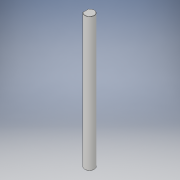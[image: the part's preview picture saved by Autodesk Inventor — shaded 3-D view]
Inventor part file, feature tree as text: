
AUTODESK INVENTOR PART (.ipt)
format: ipt  version: 2019 (Build 230136000, 136)  size: 122,880 bytes
history: native  units: in
note: dims shown in document units (in); Inventor stores cm internally (conversion verified against a paired STEP export)
features: chamfer x1, direct_edit x1, extrude x1, fillet x1, sketch x1, projected_geometry x1, other x1
ambient origin geometry x8: Origin, YZ Plane, XZ Plane, XY Plane, X Axis, Y Axis, Z Axis, Center Point
bodies: Solid1 (feature_tree)
feature tree (7):
  chamfer  "Chamfer1"  Distance=0.505in
  direct_edit  "Direct Edit2"
  extrude  "Extrusion1"  Depth=0.005in
  fillet  "Fillet1"  [1 undecoded]
  sketch  "Sketch1"  dims[d3=-0.005in d4=0.505in d5=0.0in d6=0.005in]
  projected_geometry  "Projected Loop1"
  other  "Size1"
note: 1 required parameter value undecoded (feature->parameter linkage not recoverable at this tier; creation-order binding heuristic only, values carry confidence <= 0.55)
